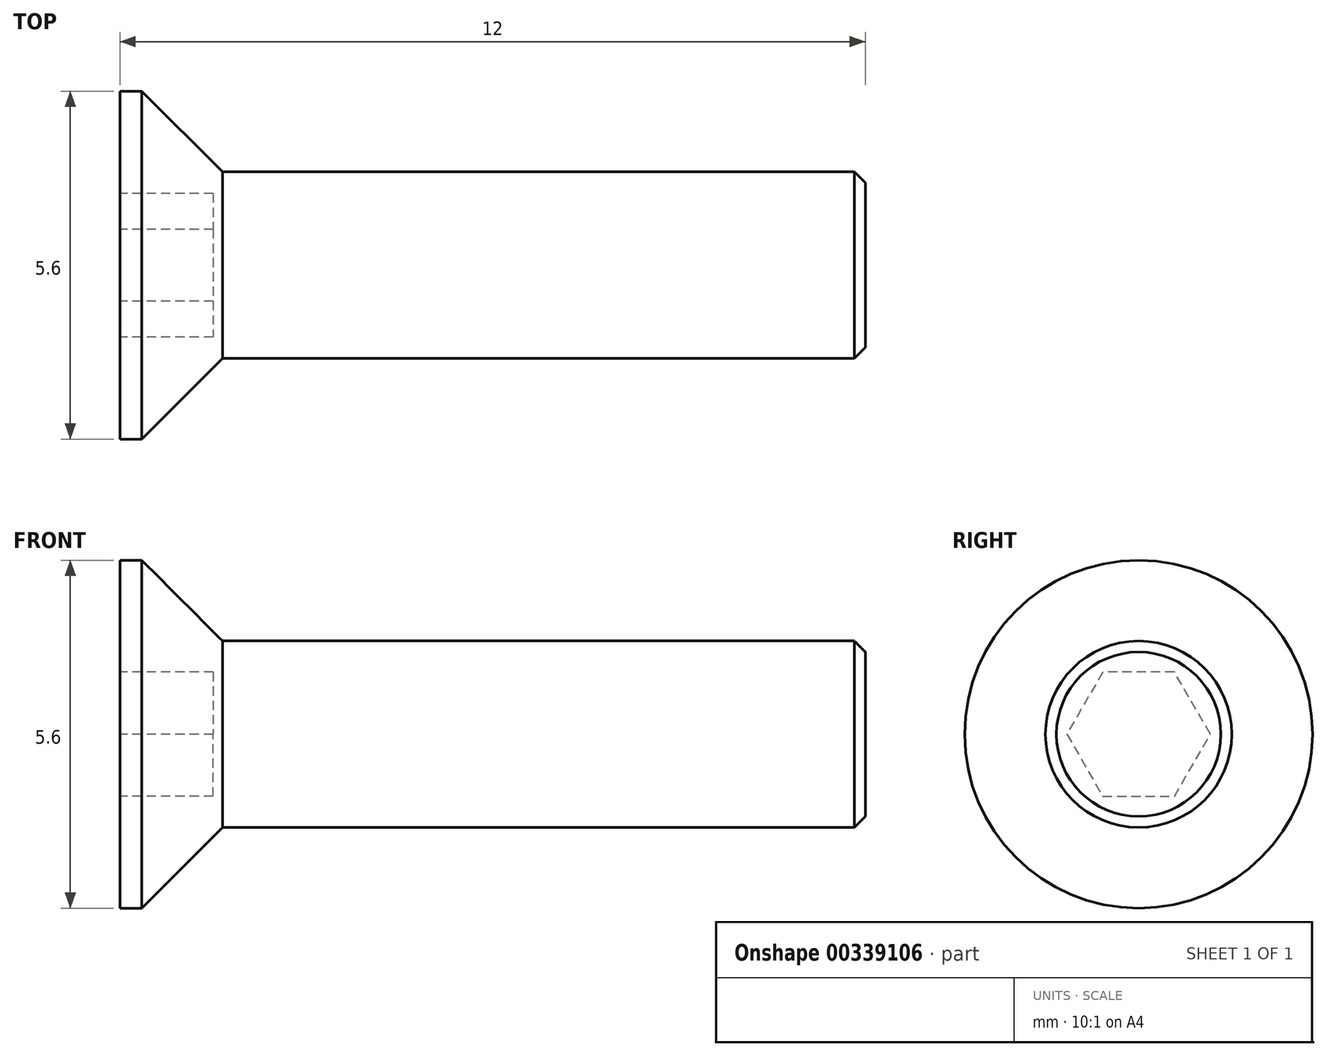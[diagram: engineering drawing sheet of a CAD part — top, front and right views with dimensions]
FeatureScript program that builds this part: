
annotation { "Feature Type Name" : "Feature", "Feature Type Description" : "" }
export const myFeature = defineFeature(function(context is Context, id is Id, definition is map)
    precondition{}
    {
        {
            var Q0;
            Q0=qCreatedBy(makeId("Front.planeOp"),FACE);
            var sketch = newSketch(context, id + "F0", { "sketchPlane" : qUnion([Q0])});
            skLineSegment(sketch, "E0", {"start": v(0, 0) * mm, "end": v(0, 2.8) * mm});
            skLineSegment(sketch, "E1", {"start": v(0, 2.8) * mm, "end": v(0.35, 2.8) * mm});
            skLineSegment(sketch, "E2", {"start": v(0.35, 2.8) * mm, "end": v(1.65, 1.5) * mm});
            skLineSegment(sketch, "E3", {"start": v(1.65, 1.5) * mm, "end": v(11.82, 1.5) * mm});
            skLineSegment(sketch, "E4", {"start": v(11.82, 1.5) * mm, "end": v(12, 1.32) * mm});
            skLineSegment(sketch, "E5", {"start": v(12, 1.32) * mm, "end": v(12, 0) * mm});
            skLineSegment(sketch, "E6", {"start": v(0, 0) * mm, "end": v(12, 0) * mm});
            skSolve(sketch);
        }
        {
            var Q0;
            Q0=makeQuery(id+"F0.imprint","IMPRINT",FACE,{"disambiguationData":[TD([[makeQuery(id+"F0.imprint","IMPRINT",EDGE,{"derivedFrom":sQuery(id+"F0.wireOp",EDGE,"E0")}),-1.0]])]});
            var Q1;
            Q1=sQuery(id+"F0.wireOp",EDGE,"E6");
            revolve(context, id + "F1", {"entities" : qUnion([Q0]), "axis" : qUnion([Q1]), "revolveType" : RevolveType.FULL});
        }
        {
            var Q0;
            Q0=makeQuery(id+"F1.opRevolve","SWEPT_FACE",FACE,{"disambiguationData":[OSD([sQuery(id+"F0.wireOp",EDGE,"E0")])]});
            var sketch = newSketch(context, id + "F2", { "sketchPlane" : qUnion([Q0])});
            skCircle(sketch, "E7.cCircle", {"center": v(0, 0) * mm, "radius": 1.15 * mm, "construction": true});
            skLineSegment(sketch, "E7.0", {"start": v(0.58, 1) * mm, "end": v(1.15, 0) * mm});
            skLineSegment(sketch, "E7.1", {"start": v(1.15, 0) * mm, "end": v(0.58, -1) * mm});
            skLineSegment(sketch, "E7.2", {"start": v(0.58, -1) * mm, "end": v(-0.58, -1) * mm});
            skLineSegment(sketch, "E7.3", {"start": v(-0.58, -1) * mm, "end": v(-1.15, 0) * mm});
            skLineSegment(sketch, "E7.4", {"start": v(-1.15, 0) * mm, "end": v(-0.58, 1) * mm});
            skLineSegment(sketch, "E7.5", {"start": v(-0.58, 1) * mm, "end": v(0.58, 1) * mm});
            skSolve(sketch);
        }
        {
            var Q0;
            Q0=makeQuery(id+"F2.imprint","IMPRINT",FACE,{"disambiguationData":[TD([[makeQuery(id+"F2.imprint","IMPRINT",EDGE,{"derivedFrom":sQuery(id+"F2.wireOp",EDGE,"E7.0")}),-1.0]])]});
            var Q1;
            Q1=sQuery(id+"F2.wireOp",EDGE,"E7.3");
            var Q2;
            Q2=sQuery(id+"F2.wireOp",EDGE,"E7.4");
            extrude(context, id + "F3", {"entities" : qUnion([Q0]), "operationType" : NewBodyOperationType.REMOVE, "surfaceEntities" : qUnion([Q1, Q2]), "oppositeDirection" : true, "depth" : 1.5 * mm});
        }
    });
